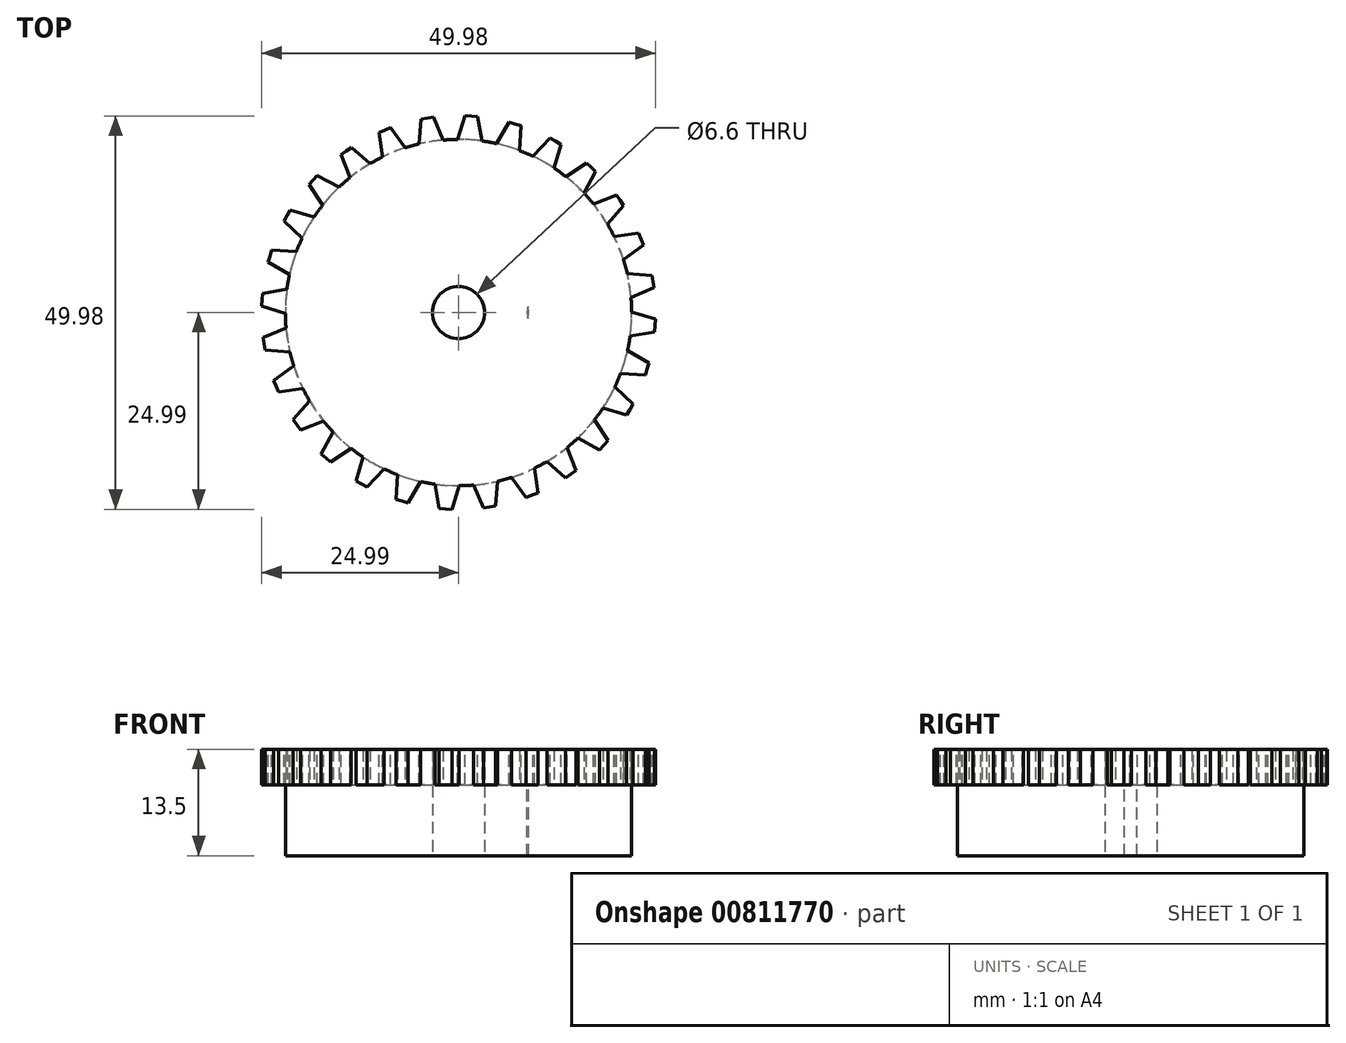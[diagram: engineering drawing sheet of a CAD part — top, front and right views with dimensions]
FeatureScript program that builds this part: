
annotation { "Feature Type Name" : "Feature", "Feature Type Description" : "" }
export const myFeature = defineFeature(function(context is Context, id is Id, definition is map)
    precondition{}
    {
        {
            var Q0;
            Q0=qCreatedBy(makeId("Top.planeOp"),FACE);
            var sketch = newSketch(context, id + "F0", { "sketchPlane" : qUnion([Q0])});
            skCircle(sketch, "E0", {"center": v(0, 0) * mm, "radius": 22 * mm});
            skLineSegment(sketch, "E1", {"start": v(-18.07, -12.55) * mm, "end": v(-20.53, -14.26) * mm, "construction": true});
            skLineSegment(sketch, "E2", {"start": v(-20.53, -14.26) * mm, "end": v(-20.07, -14.92) * mm});
            skLineSegment(sketch, "E3", {"start": v(-20.53, -14.26) * mm, "end": v(-20.99, -13.6) * mm});
            skLineSegment(sketch, "E4", {"start": v(-20.07, -14.92) * mm, "end": v(-17.6, -13.2) * mm, "construction": true});
            skLineSegment(sketch, "E5", {"start": v(-20.99, -13.6) * mm, "end": v(-18.51, -11.89) * mm, "construction": true});
            skLineSegment(sketch, "E6", {"start": v(-20.07, -14.92) * mm, "end": v(-17.14, -13.8) * mm});
            skLineSegment(sketch, "E7", {"start": v(-20.99, -13.6) * mm, "end": v(-18.9, -11.25) * mm});
            skCircle(sketch, "E8", {"center": v(0, 0) * mm, "radius": 8.87 * mm});
            skCircle(sketch, "E9", {"center": v(0, 0) * mm, "radius": 3.3 * mm});
            skLineSegment(sketch, "E10", {"start": v(-8.87, 0) * mm, "end": v(11.73, 0) * mm, "construction": true});
            skLineSegment(sketch, "E11.trimOffspring", {"start": v(-0.6, 8.85) * mm, "end": v(-0.6, 8.85) * mm});
            skCircle(sketch, "E12", {"center": v(11.73, 0) * mm, "radius": 3 * mm});
            skLineSegment(sketch, "E13", {"start": v(4.3, -7.76) * mm, "end": v(13.23, -2.6) * mm});
            skLineSegment(sketch, "E14.1.0", {"start": v(-17.43, -17.94) * mm, "end": v(-15.93, -15.17) * mm});
            skLineSegment(sketch, "E14.1.1", {"start": v(-17.43, -17.94) * mm, "end": v(-15.4, -15.7) * mm, "construction": true});
            skLineSegment(sketch, "E14.1.2", {"start": v(-14.82, -16.26) * mm, "end": v(-16.84, -18.47) * mm, "construction": true});
            skLineSegment(sketch, "E14.1.3", {"start": v(-16.25, -19.01) * mm, "end": v(-14.22, -16.79) * mm, "construction": true});
            skLineSegment(sketch, "E14.1.4", {"start": v(-16.25, -19.01) * mm, "end": v(-13.64, -17.26) * mm});
            skLineSegment(sketch, "E14.1.5", {"start": v(-16.84, -18.47) * mm, "end": v(-16.25, -19.01) * mm});
            skLineSegment(sketch, "E14.1.6", {"start": v(-16.84, -18.47) * mm, "end": v(-17.43, -17.94) * mm});
            skLineSegment(sketch, "E14.2.0", {"start": v(-13, -21.37) * mm, "end": v(-12.15, -18.34) * mm});
            skLineSegment(sketch, "E14.2.1", {"start": v(-13, -21.37) * mm, "end": v(-11.52, -18.74) * mm, "construction": true});
            skLineSegment(sketch, "E14.2.2", {"start": v(-10.83, -19.15) * mm, "end": v(-12.3, -21.76) * mm, "construction": true});
            skLineSegment(sketch, "E14.2.3", {"start": v(-11.61, -22.15) * mm, "end": v(-10.13, -19.53) * mm, "construction": true});
            skLineSegment(sketch, "E14.2.4", {"start": v(-11.61, -22.15) * mm, "end": v(-9.46, -19.86) * mm});
            skLineSegment(sketch, "E14.2.5", {"start": v(-12.3, -21.76) * mm, "end": v(-11.61, -22.15) * mm});
            skLineSegment(sketch, "E14.2.6", {"start": v(-12.3, -21.76) * mm, "end": v(-13, -21.37) * mm});
            skLineSegment(sketch, "E15.1.3.0", {"start": v(-7.93, -23.72) * mm, "end": v(-7.77, -20.58) * mm});
            skLineSegment(sketch, "E15.3.3.0", {"start": v(-7.93, -23.72) * mm, "end": v(-7.06, -20.84) * mm, "construction": true});
            skLineSegment(sketch, "E15.6.3.0", {"start": v(-6.3, -21.08) * mm, "end": v(-7.16, -23.95) * mm, "construction": true});
            skLineSegment(sketch, "E15.9.3.0", {"start": v(-6.4, -24.18) * mm, "end": v(-5.53, -21.3) * mm, "construction": true});
            skLineSegment(sketch, "E15.12.3.0", {"start": v(-6.4, -24.18) * mm, "end": v(-4.8, -21.47) * mm});
            skLineSegment(sketch, "E15.15.3.0", {"start": v(-7.16, -23.95) * mm, "end": v(-6.4, -24.18) * mm});
            skLineSegment(sketch, "E15.18.3.0", {"start": v(-7.16, -23.95) * mm, "end": v(-7.93, -23.72) * mm});
            skLineSegment(sketch, "E15.1.4.0", {"start": v(-2.45, -24.9) * mm, "end": v(-3, -21.8) * mm});
            skLineSegment(sketch, "E15.3.4.0", {"start": v(-2.45, -24.9) * mm, "end": v(-2.25, -21.88) * mm, "construction": true});
            skLineSegment(sketch, "E15.6.4.0", {"start": v(-1.45, -21.95) * mm, "end": v(-1.65, -24.95) * mm, "construction": true});
            skLineSegment(sketch, "E15.9.4.0", {"start": v(-0.85, -25) * mm, "end": v(-0.65, -22) * mm, "construction": true});
            skLineSegment(sketch, "E15.12.4.0", {"start": v(-0.85, -25) * mm, "end": v(0.1, -22) * mm});
            skLineSegment(sketch, "E15.15.4.0", {"start": v(-1.65, -24.95) * mm, "end": v(-0.85, -25) * mm});
            skLineSegment(sketch, "E15.18.4.0", {"start": v(-1.65, -24.95) * mm, "end": v(-2.45, -24.9) * mm});
            skLineSegment(sketch, "E15.1.5.0", {"start": v(3.15, -24.81) * mm, "end": v(1.93, -21.92) * mm});
            skLineSegment(sketch, "E15.3.5.0", {"start": v(3.15, -24.81) * mm, "end": v(2.68, -21.84) * mm, "construction": true});
            skLineSegment(sketch, "E15.6.5.0", {"start": v(3.47, -21.72) * mm, "end": v(3.94, -24.69) * mm, "construction": true});
            skLineSegment(sketch, "E15.9.5.0", {"start": v(4.73, -24.56) * mm, "end": v(4.26, -21.58) * mm, "construction": true});
            skLineSegment(sketch, "E15.12.5.0", {"start": v(4.73, -24.56) * mm, "end": v(5, -21.43) * mm});
            skLineSegment(sketch, "E15.15.5.0", {"start": v(3.94, -24.69) * mm, "end": v(4.73, -24.56) * mm});
            skLineSegment(sketch, "E15.18.5.0", {"start": v(3.94, -24.69) * mm, "end": v(3.15, -24.81) * mm});
            skLineSegment(sketch, "E15.1.6.0", {"start": v(8.6, -23.49) * mm, "end": v(6.76, -20.94) * mm});
            skLineSegment(sketch, "E15.3.6.0", {"start": v(8.6, -23.49) * mm, "end": v(7.47, -20.7) * mm, "construction": true});
            skLineSegment(sketch, "E15.6.6.0", {"start": v(8.22, -20.4) * mm, "end": v(9.34, -23.2) * mm, "construction": true});
            skLineSegment(sketch, "E15.9.6.0", {"start": v(10.08, -22.9) * mm, "end": v(8.95, -20.1) * mm, "construction": true});
            skLineSegment(sketch, "E15.12.6.0", {"start": v(10.08, -22.9) * mm, "end": v(9.63, -19.78) * mm});
            skLineSegment(sketch, "E15.15.6.0", {"start": v(9.34, -23.2) * mm, "end": v(10.08, -22.9) * mm});
            skLineSegment(sketch, "E15.18.6.0", {"start": v(9.34, -23.2) * mm, "end": v(8.6, -23.49) * mm});
            skLineSegment(sketch, "E15.1.7.0", {"start": v(13.6, -20.99) * mm, "end": v(11.25, -18.9) * mm});
            skLineSegment(sketch, "E15.3.7.0", {"start": v(13.6, -20.99) * mm, "end": v(11.89, -18.51) * mm, "construction": true});
            skLineSegment(sketch, "E15.6.7.0", {"start": v(12.55, -18.07) * mm, "end": v(14.26, -20.53) * mm, "construction": true});
            skLineSegment(sketch, "E15.9.7.0", {"start": v(14.92, -20.07) * mm, "end": v(13.2, -17.6) * mm, "construction": true});
            skLineSegment(sketch, "E15.12.7.0", {"start": v(14.92, -20.07) * mm, "end": v(13.8, -17.14) * mm});
            skLineSegment(sketch, "E15.15.7.0", {"start": v(14.26, -20.53) * mm, "end": v(14.92, -20.07) * mm});
            skLineSegment(sketch, "E15.18.7.0", {"start": v(14.26, -20.53) * mm, "end": v(13.6, -20.99) * mm});
            skLineSegment(sketch, "E15.1.8.0", {"start": v(17.94, -17.43) * mm, "end": v(15.17, -15.93) * mm});
            skLineSegment(sketch, "E15.3.8.0", {"start": v(17.94, -17.43) * mm, "end": v(15.7, -15.4) * mm, "construction": true});
            skLineSegment(sketch, "E15.6.8.0", {"start": v(16.26, -14.82) * mm, "end": v(18.47, -16.84) * mm, "construction": true});
            skLineSegment(sketch, "E15.9.8.0", {"start": v(19.01, -16.25) * mm, "end": v(16.79, -14.22) * mm, "construction": true});
            skLineSegment(sketch, "E15.12.8.0", {"start": v(19.01, -16.25) * mm, "end": v(17.26, -13.64) * mm});
            skLineSegment(sketch, "E15.15.8.0", {"start": v(18.47, -16.84) * mm, "end": v(19.01, -16.25) * mm});
            skLineSegment(sketch, "E15.18.8.0", {"start": v(18.47, -16.84) * mm, "end": v(17.94, -17.43) * mm});
            skLineSegment(sketch, "E15.1.9.0", {"start": v(21.37, -13) * mm, "end": v(18.34, -12.15) * mm});
            skLineSegment(sketch, "E15.3.9.0", {"start": v(21.37, -13) * mm, "end": v(18.74, -11.52) * mm, "construction": true});
            skLineSegment(sketch, "E15.6.9.0", {"start": v(19.15, -10.83) * mm, "end": v(21.76, -12.3) * mm, "construction": true});
            skLineSegment(sketch, "E15.9.9.0", {"start": v(22.15, -11.61) * mm, "end": v(19.53, -10.13) * mm, "construction": true});
            skLineSegment(sketch, "E15.12.9.0", {"start": v(22.15, -11.61) * mm, "end": v(19.86, -9.46) * mm});
            skLineSegment(sketch, "E15.15.9.0", {"start": v(21.76, -12.3) * mm, "end": v(22.15, -11.61) * mm});
            skLineSegment(sketch, "E15.18.9.0", {"start": v(21.76, -12.3) * mm, "end": v(21.37, -13) * mm});
            skLineSegment(sketch, "E15.1.10.0", {"start": v(23.72, -7.93) * mm, "end": v(20.58, -7.77) * mm});
            skLineSegment(sketch, "E15.3.10.0", {"start": v(23.72, -7.93) * mm, "end": v(20.84, -7.06) * mm, "construction": true});
            skLineSegment(sketch, "E15.6.10.0", {"start": v(21.08, -6.3) * mm, "end": v(23.95, -7.16) * mm, "construction": true});
            skLineSegment(sketch, "E15.9.10.0", {"start": v(24.18, -6.4) * mm, "end": v(21.3, -5.53) * mm, "construction": true});
            skLineSegment(sketch, "E15.12.10.0", {"start": v(24.18, -6.4) * mm, "end": v(21.47, -4.8) * mm});
            skLineSegment(sketch, "E15.15.10.0", {"start": v(23.95, -7.16) * mm, "end": v(24.18, -6.4) * mm});
            skLineSegment(sketch, "E15.18.10.0", {"start": v(23.95, -7.16) * mm, "end": v(23.72, -7.93) * mm});
            skLineSegment(sketch, "E15.1.11.0", {"start": v(24.9, -2.45) * mm, "end": v(21.8, -3) * mm});
            skLineSegment(sketch, "E15.3.11.0", {"start": v(24.9, -2.45) * mm, "end": v(21.88, -2.25) * mm, "construction": true});
            skLineSegment(sketch, "E15.6.11.0", {"start": v(21.95, -1.45) * mm, "end": v(24.95, -1.65) * mm, "construction": true});
            skLineSegment(sketch, "E15.9.11.0", {"start": v(25, -0.85) * mm, "end": v(22, -0.65) * mm, "construction": true});
            skLineSegment(sketch, "E15.12.11.0", {"start": v(25, -0.85) * mm, "end": v(22, 0.1) * mm});
            skLineSegment(sketch, "E15.15.11.0", {"start": v(24.95, -1.65) * mm, "end": v(25, -0.85) * mm});
            skLineSegment(sketch, "E15.18.11.0", {"start": v(24.95, -1.65) * mm, "end": v(24.9, -2.45) * mm});
            skLineSegment(sketch, "E15.1.12.0", {"start": v(24.81, 3.15) * mm, "end": v(21.92, 1.93) * mm});
            skLineSegment(sketch, "E15.3.12.0", {"start": v(24.81, 3.15) * mm, "end": v(21.84, 2.68) * mm, "construction": true});
            skLineSegment(sketch, "E15.6.12.0", {"start": v(21.72, 3.47) * mm, "end": v(24.69, 3.94) * mm, "construction": true});
            skLineSegment(sketch, "E15.9.12.0", {"start": v(24.56, 4.73) * mm, "end": v(21.58, 4.26) * mm, "construction": true});
            skLineSegment(sketch, "E15.12.12.0", {"start": v(24.56, 4.73) * mm, "end": v(21.43, 5) * mm});
            skLineSegment(sketch, "E15.15.12.0", {"start": v(24.69, 3.94) * mm, "end": v(24.56, 4.73) * mm});
            skLineSegment(sketch, "E15.18.12.0", {"start": v(24.69, 3.94) * mm, "end": v(24.81, 3.15) * mm});
            skLineSegment(sketch, "E15.1.13.0", {"start": v(23.49, 8.6) * mm, "end": v(20.94, 6.76) * mm});
            skLineSegment(sketch, "E15.3.13.0", {"start": v(23.49, 8.6) * mm, "end": v(20.7, 7.47) * mm, "construction": true});
            skLineSegment(sketch, "E15.6.13.0", {"start": v(20.4, 8.22) * mm, "end": v(23.2, 9.34) * mm, "construction": true});
            skLineSegment(sketch, "E15.9.13.0", {"start": v(22.9, 10.08) * mm, "end": v(20.1, 8.95) * mm, "construction": true});
            skLineSegment(sketch, "E15.12.13.0", {"start": v(22.9, 10.08) * mm, "end": v(19.78, 9.63) * mm});
            skLineSegment(sketch, "E15.15.13.0", {"start": v(23.2, 9.34) * mm, "end": v(22.9, 10.08) * mm});
            skLineSegment(sketch, "E15.18.13.0", {"start": v(23.2, 9.34) * mm, "end": v(23.49, 8.6) * mm});
            skLineSegment(sketch, "E15.1.14.0", {"start": v(20.99, 13.6) * mm, "end": v(18.9, 11.25) * mm});
            skLineSegment(sketch, "E15.3.14.0", {"start": v(20.99, 13.6) * mm, "end": v(18.51, 11.89) * mm, "construction": true});
            skLineSegment(sketch, "E15.6.14.0", {"start": v(18.07, 12.55) * mm, "end": v(20.53, 14.26) * mm, "construction": true});
            skLineSegment(sketch, "E15.9.14.0", {"start": v(20.07, 14.92) * mm, "end": v(17.6, 13.2) * mm, "construction": true});
            skLineSegment(sketch, "E15.12.14.0", {"start": v(20.07, 14.92) * mm, "end": v(17.14, 13.8) * mm});
            skLineSegment(sketch, "E15.15.14.0", {"start": v(20.53, 14.26) * mm, "end": v(20.07, 14.92) * mm});
            skLineSegment(sketch, "E15.18.14.0", {"start": v(20.53, 14.26) * mm, "end": v(20.99, 13.6) * mm});
            skLineSegment(sketch, "E15.1.15.0", {"start": v(17.43, 17.94) * mm, "end": v(15.93, 15.17) * mm});
            skLineSegment(sketch, "E15.3.15.0", {"start": v(17.43, 17.94) * mm, "end": v(15.4, 15.7) * mm, "construction": true});
            skLineSegment(sketch, "E15.6.15.0", {"start": v(14.82, 16.26) * mm, "end": v(16.84, 18.47) * mm, "construction": true});
            skLineSegment(sketch, "E15.9.15.0", {"start": v(16.25, 19.01) * mm, "end": v(14.22, 16.79) * mm, "construction": true});
            skLineSegment(sketch, "E15.12.15.0", {"start": v(16.25, 19.01) * mm, "end": v(13.64, 17.26) * mm});
            skLineSegment(sketch, "E15.15.15.0", {"start": v(16.84, 18.47) * mm, "end": v(16.25, 19.01) * mm});
            skLineSegment(sketch, "E15.18.15.0", {"start": v(16.84, 18.47) * mm, "end": v(17.43, 17.94) * mm});
            skLineSegment(sketch, "E15.1.16.0", {"start": v(13, 21.37) * mm, "end": v(12.15, 18.34) * mm});
            skLineSegment(sketch, "E15.3.16.0", {"start": v(13, 21.37) * mm, "end": v(11.52, 18.74) * mm, "construction": true});
            skLineSegment(sketch, "E15.6.16.0", {"start": v(10.83, 19.15) * mm, "end": v(12.3, 21.76) * mm, "construction": true});
            skLineSegment(sketch, "E15.9.16.0", {"start": v(11.61, 22.15) * mm, "end": v(10.13, 19.53) * mm, "construction": true});
            skLineSegment(sketch, "E15.12.16.0", {"start": v(11.61, 22.15) * mm, "end": v(9.46, 19.86) * mm});
            skLineSegment(sketch, "E15.15.16.0", {"start": v(12.3, 21.76) * mm, "end": v(11.61, 22.15) * mm});
            skLineSegment(sketch, "E15.18.16.0", {"start": v(12.3, 21.76) * mm, "end": v(13, 21.37) * mm});
            skLineSegment(sketch, "E15.1.17.0", {"start": v(7.93, 23.72) * mm, "end": v(7.77, 20.58) * mm});
            skLineSegment(sketch, "E15.3.17.0", {"start": v(7.93, 23.72) * mm, "end": v(7.06, 20.84) * mm, "construction": true});
            skLineSegment(sketch, "E15.6.17.0", {"start": v(6.3, 21.08) * mm, "end": v(7.16, 23.95) * mm, "construction": true});
            skLineSegment(sketch, "E15.9.17.0", {"start": v(6.4, 24.18) * mm, "end": v(5.53, 21.3) * mm, "construction": true});
            skLineSegment(sketch, "E15.12.17.0", {"start": v(6.4, 24.18) * mm, "end": v(4.8, 21.47) * mm});
            skLineSegment(sketch, "E15.15.17.0", {"start": v(7.16, 23.95) * mm, "end": v(6.4, 24.18) * mm});
            skLineSegment(sketch, "E15.18.17.0", {"start": v(7.16, 23.95) * mm, "end": v(7.93, 23.72) * mm});
            skLineSegment(sketch, "E15.1.18.0", {"start": v(2.45, 24.9) * mm, "end": v(3, 21.8) * mm});
            skLineSegment(sketch, "E15.3.18.0", {"start": v(2.45, 24.9) * mm, "end": v(2.25, 21.88) * mm, "construction": true});
            skLineSegment(sketch, "E15.6.18.0", {"start": v(1.45, 21.95) * mm, "end": v(1.65, 24.95) * mm, "construction": true});
            skLineSegment(sketch, "E15.9.18.0", {"start": v(0.85, 25) * mm, "end": v(0.65, 22) * mm, "construction": true});
            skLineSegment(sketch, "E15.12.18.0", {"start": v(0.85, 25) * mm, "end": v(-0.1, 22) * mm});
            skLineSegment(sketch, "E15.15.18.0", {"start": v(1.65, 24.95) * mm, "end": v(0.85, 25) * mm});
            skLineSegment(sketch, "E15.18.18.0", {"start": v(1.65, 24.95) * mm, "end": v(2.45, 24.9) * mm});
            skLineSegment(sketch, "E15.1.19.0", {"start": v(-3.15, 24.81) * mm, "end": v(-1.93, 21.92) * mm});
            skLineSegment(sketch, "E15.3.19.0", {"start": v(-3.15, 24.81) * mm, "end": v(-2.68, 21.84) * mm, "construction": true});
            skLineSegment(sketch, "E15.6.19.0", {"start": v(-3.47, 21.72) * mm, "end": v(-3.94, 24.69) * mm, "construction": true});
            skLineSegment(sketch, "E15.9.19.0", {"start": v(-4.73, 24.56) * mm, "end": v(-4.26, 21.58) * mm, "construction": true});
            skLineSegment(sketch, "E15.12.19.0", {"start": v(-4.73, 24.56) * mm, "end": v(-5, 21.43) * mm});
            skLineSegment(sketch, "E15.15.19.0", {"start": v(-3.94, 24.69) * mm, "end": v(-4.73, 24.56) * mm});
            skLineSegment(sketch, "E15.18.19.0", {"start": v(-3.94, 24.69) * mm, "end": v(-3.15, 24.81) * mm});
            skLineSegment(sketch, "E15.1.20.0", {"start": v(-8.6, 23.49) * mm, "end": v(-6.76, 20.94) * mm});
            skLineSegment(sketch, "E15.3.20.0", {"start": v(-8.6, 23.49) * mm, "end": v(-7.47, 20.7) * mm, "construction": true});
            skLineSegment(sketch, "E15.6.20.0", {"start": v(-8.22, 20.4) * mm, "end": v(-9.34, 23.2) * mm, "construction": true});
            skLineSegment(sketch, "E15.9.20.0", {"start": v(-10.08, 22.9) * mm, "end": v(-8.95, 20.1) * mm, "construction": true});
            skLineSegment(sketch, "E15.12.20.0", {"start": v(-10.08, 22.9) * mm, "end": v(-9.63, 19.78) * mm});
            skLineSegment(sketch, "E15.15.20.0", {"start": v(-9.34, 23.2) * mm, "end": v(-10.08, 22.9) * mm});
            skLineSegment(sketch, "E15.18.20.0", {"start": v(-9.34, 23.2) * mm, "end": v(-8.6, 23.49) * mm});
            skLineSegment(sketch, "E15.1.21.0", {"start": v(-13.6, 20.99) * mm, "end": v(-11.25, 18.9) * mm});
            skLineSegment(sketch, "E15.3.21.0", {"start": v(-13.6, 20.99) * mm, "end": v(-11.89, 18.51) * mm, "construction": true});
            skLineSegment(sketch, "E15.6.21.0", {"start": v(-12.55, 18.07) * mm, "end": v(-14.26, 20.53) * mm, "construction": true});
            skLineSegment(sketch, "E15.9.21.0", {"start": v(-14.92, 20.07) * mm, "end": v(-13.2, 17.6) * mm, "construction": true});
            skLineSegment(sketch, "E15.12.21.0", {"start": v(-14.92, 20.07) * mm, "end": v(-13.8, 17.14) * mm});
            skLineSegment(sketch, "E15.15.21.0", {"start": v(-14.26, 20.53) * mm, "end": v(-14.92, 20.07) * mm});
            skLineSegment(sketch, "E15.18.21.0", {"start": v(-14.26, 20.53) * mm, "end": v(-13.6, 20.99) * mm});
            skLineSegment(sketch, "E15.1.22.0", {"start": v(-17.94, 17.43) * mm, "end": v(-15.17, 15.93) * mm});
            skLineSegment(sketch, "E15.3.22.0", {"start": v(-17.94, 17.43) * mm, "end": v(-15.7, 15.4) * mm, "construction": true});
            skLineSegment(sketch, "E15.6.22.0", {"start": v(-16.26, 14.82) * mm, "end": v(-18.47, 16.84) * mm, "construction": true});
            skLineSegment(sketch, "E15.9.22.0", {"start": v(-19.01, 16.25) * mm, "end": v(-16.79, 14.22) * mm, "construction": true});
            skLineSegment(sketch, "E15.12.22.0", {"start": v(-19.01, 16.25) * mm, "end": v(-17.26, 13.64) * mm});
            skLineSegment(sketch, "E15.15.22.0", {"start": v(-18.47, 16.84) * mm, "end": v(-19.01, 16.25) * mm});
            skLineSegment(sketch, "E15.18.22.0", {"start": v(-18.47, 16.84) * mm, "end": v(-17.94, 17.43) * mm});
            skLineSegment(sketch, "E15.1.23.0", {"start": v(-21.37, 13) * mm, "end": v(-18.34, 12.15) * mm});
            skLineSegment(sketch, "E15.3.23.0", {"start": v(-21.37, 13) * mm, "end": v(-18.74, 11.52) * mm, "construction": true});
            skLineSegment(sketch, "E15.6.23.0", {"start": v(-19.15, 10.83) * mm, "end": v(-21.76, 12.3) * mm, "construction": true});
            skLineSegment(sketch, "E15.9.23.0", {"start": v(-22.15, 11.61) * mm, "end": v(-19.53, 10.13) * mm, "construction": true});
            skLineSegment(sketch, "E15.12.23.0", {"start": v(-22.15, 11.61) * mm, "end": v(-19.86, 9.46) * mm});
            skLineSegment(sketch, "E15.15.23.0", {"start": v(-21.76, 12.3) * mm, "end": v(-22.15, 11.61) * mm});
            skLineSegment(sketch, "E15.18.23.0", {"start": v(-21.76, 12.3) * mm, "end": v(-21.37, 13) * mm});
            skLineSegment(sketch, "E15.1.24.0", {"start": v(-23.72, 7.93) * mm, "end": v(-20.58, 7.77) * mm});
            skLineSegment(sketch, "E15.3.24.0", {"start": v(-23.72, 7.93) * mm, "end": v(-20.84, 7.06) * mm, "construction": true});
            skLineSegment(sketch, "E15.6.24.0", {"start": v(-21.08, 6.3) * mm, "end": v(-23.95, 7.16) * mm, "construction": true});
            skLineSegment(sketch, "E15.9.24.0", {"start": v(-24.18, 6.4) * mm, "end": v(-21.3, 5.53) * mm, "construction": true});
            skLineSegment(sketch, "E15.12.24.0", {"start": v(-24.18, 6.4) * mm, "end": v(-21.47, 4.8) * mm});
            skLineSegment(sketch, "E15.15.24.0", {"start": v(-23.95, 7.16) * mm, "end": v(-24.18, 6.4) * mm});
            skLineSegment(sketch, "E15.18.24.0", {"start": v(-23.95, 7.16) * mm, "end": v(-23.72, 7.93) * mm});
            skLineSegment(sketch, "E15.1.25.0", {"start": v(-24.9, 2.45) * mm, "end": v(-21.8, 3) * mm});
            skLineSegment(sketch, "E15.3.25.0", {"start": v(-24.9, 2.45) * mm, "end": v(-21.88, 2.25) * mm, "construction": true});
            skLineSegment(sketch, "E15.6.25.0", {"start": v(-21.95, 1.45) * mm, "end": v(-24.95, 1.65) * mm, "construction": true});
            skLineSegment(sketch, "E15.9.25.0", {"start": v(-25, 0.85) * mm, "end": v(-22, 0.65) * mm, "construction": true});
            skLineSegment(sketch, "E15.12.25.0", {"start": v(-25, 0.85) * mm, "end": v(-22, -0.1) * mm});
            skLineSegment(sketch, "E15.15.25.0", {"start": v(-24.95, 1.65) * mm, "end": v(-25, 0.85) * mm});
            skLineSegment(sketch, "E15.18.25.0", {"start": v(-24.95, 1.65) * mm, "end": v(-24.9, 2.45) * mm});
            skLineSegment(sketch, "E15.1.26.0", {"start": v(-24.81, -3.15) * mm, "end": v(-21.92, -1.93) * mm});
            skLineSegment(sketch, "E15.3.26.0", {"start": v(-24.81, -3.15) * mm, "end": v(-21.84, -2.68) * mm, "construction": true});
            skLineSegment(sketch, "E15.6.26.0", {"start": v(-21.72, -3.47) * mm, "end": v(-24.69, -3.94) * mm, "construction": true});
            skLineSegment(sketch, "E15.9.26.0", {"start": v(-24.56, -4.73) * mm, "end": v(-21.58, -4.26) * mm, "construction": true});
            skLineSegment(sketch, "E15.12.26.0", {"start": v(-24.56, -4.73) * mm, "end": v(-21.43, -5) * mm});
            skLineSegment(sketch, "E15.15.26.0", {"start": v(-24.69, -3.94) * mm, "end": v(-24.56, -4.73) * mm});
            skLineSegment(sketch, "E15.18.26.0", {"start": v(-24.69, -3.94) * mm, "end": v(-24.81, -3.15) * mm});
            skLineSegment(sketch, "E15.1.27.0", {"start": v(-23.49, -8.6) * mm, "end": v(-20.94, -6.76) * mm});
            skLineSegment(sketch, "E15.3.27.0", {"start": v(-23.49, -8.6) * mm, "end": v(-20.7, -7.47) * mm, "construction": true});
            skLineSegment(sketch, "E15.6.27.0", {"start": v(-20.4, -8.22) * mm, "end": v(-23.2, -9.34) * mm, "construction": true});
            skLineSegment(sketch, "E15.9.27.0", {"start": v(-22.9, -10.08) * mm, "end": v(-20.1, -8.95) * mm, "construction": true});
            skLineSegment(sketch, "E15.12.27.0", {"start": v(-22.9, -10.08) * mm, "end": v(-19.78, -9.63) * mm});
            skLineSegment(sketch, "E15.15.27.0", {"start": v(-23.2, -9.34) * mm, "end": v(-22.9, -10.08) * mm});
            skLineSegment(sketch, "E15.18.27.0", {"start": v(-23.2, -9.34) * mm, "end": v(-23.49, -8.6) * mm});
            skLineSegment(sketch, "E16", {"start": v(4.3, -7.76) * mm, "end": v(4.3, 7.76) * mm, "construction": true});
            skLineSegment(sketch, "E17", {"start": v(4.3, 7.76) * mm, "end": v(13.23, 2.6) * mm});
            skSolve(sketch);
        }
        {
            var Q0;
            {var subQ0=sQuery(id+"F0.wireOp",EDGE,"E15.1.20.0");Q0=makeQuery(id+"F0.imprint","IMPRINT",FACE,{"disambiguationData":[TD([[makeQuery(id+"F0.imprint","IMPRINT",EDGE,{"derivedFrom":subQ0}),-1.0]])]});}
            var Q1;
            {var subQ0=sQuery(id+"F0.wireOp",EDGE,"E12");var subQ1=makeQuery(id+"F0.imprint","INTERSECT",VERTEX,{"derivedFrom":[subQ0,sQuery(id+"F0.wireOp",EDGE,"KuiEAQZw-HmBo-JUDk-2FJ1-OJibavO7FM1e")]});Q1=makeQuery(id+"F0.imprint","IMPRINT",FACE,{"disambiguationData":[TD([[makeQuery(id+"F0.imprint","IMPRINT",EDGE,{"disambiguationData":[TD([[subQ1,-1.0]])],"derivedFrom":subQ0}),1.0]])]});}
            var Q2;
            {var subQ1=sQuery(id+"F0.wireOp",EDGE,"E15.1.22.0");Q2=makeQuery(id+"F0.imprint","IMPRINT",FACE,{"disambiguationData":[TD([[makeQuery(id+"F0.imprint","IMPRINT",EDGE,{"derivedFrom":subQ1}),-1.0]])]});}
            var Q3;
            {var subQ1=sQuery(id+"F0.wireOp",EDGE,"E15.1.14.0");Q3=makeQuery(id+"F0.imprint","IMPRINT",FACE,{"disambiguationData":[TD([[makeQuery(id+"F0.imprint","IMPRINT",EDGE,{"derivedFrom":subQ1}),-1.0]])]});}
            var Q4;
            {var subQ1=sQuery(id+"F0.wireOp",EDGE,"E15.1.24.0");Q4=makeQuery(id+"F0.imprint","IMPRINT",FACE,{"disambiguationData":[TD([[makeQuery(id+"F0.imprint","IMPRINT",EDGE,{"derivedFrom":subQ1}),-1.0]])]});}
            var Q5;
            {var subQ1=sQuery(id+"F0.wireOp",EDGE,"E15.1.13.0");Q5=makeQuery(id+"F0.imprint","IMPRINT",FACE,{"disambiguationData":[TD([[makeQuery(id+"F0.imprint","IMPRINT",EDGE,{"derivedFrom":subQ1}),-1.0]])]});}
            var Q6;
            {var subQ1=sQuery(id+"F0.wireOp",EDGE,"E15.1.4.0");Q6=makeQuery(id+"F0.imprint","IMPRINT",FACE,{"disambiguationData":[TD([[makeQuery(id+"F0.imprint","IMPRINT",EDGE,{"derivedFrom":subQ1}),-1.0]])]});}
            var Q7;
            {var subQ1=sQuery(id+"F0.wireOp",EDGE,"E15.1.12.0");Q7=makeQuery(id+"F0.imprint","IMPRINT",FACE,{"disambiguationData":[TD([[makeQuery(id+"F0.imprint","IMPRINT",EDGE,{"derivedFrom":subQ1}),-1.0]])]});}
            var Q8;
            {var subQ0=sQuery(id+"F0.wireOp",EDGE,"E15.1.8.0");Q8=makeQuery(id+"F0.imprint","IMPRINT",FACE,{"disambiguationData":[TD([[makeQuery(id+"F0.imprint","IMPRINT",EDGE,{"derivedFrom":subQ0}),-1.0]])]});}
            var Q9;
            Q9=makeQuery(id+"F0.imprint","IMPRINT",FACE,{"disambiguationData":[TD([[makeQuery(id+"F0.imprint","IMPRINT",EDGE,{"derivedFrom":sQuery(id+"F0.wireOp",EDGE,"E2")}),1.0]])]});
            var Q10;
            Q10=makeQuery(id+"F0.imprint","IMPRINT",FACE,{"disambiguationData":[TD([[makeQuery(id+"F0.imprint","IMPRINT",EDGE,{"derivedFrom":sQuery(id+"F0.wireOp",EDGE,"E9")}),-1.0]])]});
            var Q11;
            {var subQ1=sQuery(id+"F0.wireOp",EDGE,"E15.1.27.0");Q11=makeQuery(id+"F0.imprint","IMPRINT",FACE,{"disambiguationData":[TD([[makeQuery(id+"F0.imprint","IMPRINT",EDGE,{"derivedFrom":subQ1}),-1.0]])]});}
            var Q12;
            {var subQ1=sQuery(id+"F0.wireOp",EDGE,"E15.1.26.0");Q12=makeQuery(id+"F0.imprint","IMPRINT",FACE,{"disambiguationData":[TD([[makeQuery(id+"F0.imprint","IMPRINT",EDGE,{"derivedFrom":subQ1}),-1.0]])]});}
            var Q13;
            {var subQ1=sQuery(id+"F0.wireOp",EDGE,"E14.1.0");Q13=makeQuery(id+"F0.imprint","IMPRINT",FACE,{"disambiguationData":[TD([[makeQuery(id+"F0.imprint","IMPRINT",EDGE,{"derivedFrom":subQ1}),-1.0]])]});}
            var Q14;
            {var subQ1=sQuery(id+"F0.wireOp",EDGE,"E15.1.21.0");Q14=makeQuery(id+"F0.imprint","IMPRINT",FACE,{"disambiguationData":[TD([[makeQuery(id+"F0.imprint","IMPRINT",EDGE,{"derivedFrom":subQ1}),-1.0]])]});}
            var Q15;
            {var subQ0=sQuery(id+"F0.wireOp",EDGE,"KuiEAQZw-HmBo-JUDk-2FJ1-OJibavO7FM1e");var subQ1=sQuery(id+"F0.wireOp",EDGE,"E8");var subQ2=makeQuery(id+"F0.imprint","INTERSECT",VERTEX,{"derivedFrom":[subQ1,subQ0]});Q15=makeQuery(id+"F0.imprint","IMPRINT",FACE,{"disambiguationData":[TD([[makeQuery(id+"F0.imprint","IMPRINT",EDGE,{"disambiguationData":[TD([[subQ2,1.0]])],"derivedFrom":subQ1}),-1.0]])]});}
            var Q16;
            {var subQ0=sQuery(id+"F0.wireOp",EDGE,"E14.2.0");Q16=makeQuery(id+"F0.imprint","IMPRINT",FACE,{"disambiguationData":[TD([[makeQuery(id+"F0.imprint","IMPRINT",EDGE,{"derivedFrom":subQ0}),-1.0]])]});}
            var Q17;
            {var subQ1=sQuery(id+"F0.wireOp",EDGE,"E15.1.7.0");Q17=makeQuery(id+"F0.imprint","IMPRINT",FACE,{"disambiguationData":[TD([[makeQuery(id+"F0.imprint","IMPRINT",EDGE,{"derivedFrom":subQ1}),-1.0]])]});}
            var Q18;
            {var subQ0=sQuery(id+"F0.wireOp",EDGE,"E0");var subQ33=makeQuery(id+"F0.imprint","INTERSECT",VERTEX,{"derivedFrom":[subQ0,sQuery(id+"F0.wireOp",EDGE,"E15.12.11.0")]});Q18=makeQuery(id+"F0.imprint","IMPRINT",FACE,{"disambiguationData":[TD([[makeQuery(id+"F0.imprint","IMPRINT",EDGE,{"disambiguationData":[TD([[subQ33,-1.0]])],"derivedFrom":subQ0}),1.0]])]});}
            var Q19;
            {var subQ0=sQuery(id+"F0.wireOp",EDGE,"E15.1.25.0");Q19=makeQuery(id+"F0.imprint","IMPRINT",FACE,{"disambiguationData":[TD([[makeQuery(id+"F0.imprint","IMPRINT",EDGE,{"derivedFrom":subQ0}),-1.0]])]});}
            var Q20;
            {var subQ0=sQuery(id+"F0.wireOp",EDGE,"E15.1.15.0");Q20=makeQuery(id+"F0.imprint","IMPRINT",FACE,{"disambiguationData":[TD([[makeQuery(id+"F0.imprint","IMPRINT",EDGE,{"derivedFrom":subQ0}),-1.0]])]});}
            var Q21;
            {var subQ1=sQuery(id+"F0.wireOp",EDGE,"E15.1.9.0");Q21=makeQuery(id+"F0.imprint","IMPRINT",FACE,{"disambiguationData":[TD([[makeQuery(id+"F0.imprint","IMPRINT",EDGE,{"derivedFrom":subQ1}),-1.0]])]});}
            var Q22;
            {var subQ1=sQuery(id+"F0.wireOp",EDGE,"E15.1.5.0");Q22=makeQuery(id+"F0.imprint","IMPRINT",FACE,{"disambiguationData":[TD([[makeQuery(id+"F0.imprint","IMPRINT",EDGE,{"derivedFrom":subQ1}),-1.0]])]});}
            var Q23;
            {var subQ1=sQuery(id+"F0.wireOp",EDGE,"E15.1.16.0");Q23=makeQuery(id+"F0.imprint","IMPRINT",FACE,{"disambiguationData":[TD([[makeQuery(id+"F0.imprint","IMPRINT",EDGE,{"derivedFrom":subQ1}),-1.0]])]});}
            var Q24;
            {var subQ1=sQuery(id+"F0.wireOp",EDGE,"E15.1.17.0");Q24=makeQuery(id+"F0.imprint","IMPRINT",FACE,{"disambiguationData":[TD([[makeQuery(id+"F0.imprint","IMPRINT",EDGE,{"derivedFrom":subQ1}),-1.0]])]});}
            var Q25;
            {var subQ1=sQuery(id+"F0.wireOp",EDGE,"E15.1.19.0");Q25=makeQuery(id+"F0.imprint","IMPRINT",FACE,{"disambiguationData":[TD([[makeQuery(id+"F0.imprint","IMPRINT",EDGE,{"derivedFrom":subQ1}),-1.0]])]});}
            var Q26;
            {var subQ1=sQuery(id+"F0.wireOp",EDGE,"E15.1.23.0");Q26=makeQuery(id+"F0.imprint","IMPRINT",FACE,{"disambiguationData":[TD([[makeQuery(id+"F0.imprint","IMPRINT",EDGE,{"derivedFrom":subQ1}),-1.0]])]});}
            var Q27;
            {var subQ1=sQuery(id+"F0.wireOp",EDGE,"E15.1.6.0");Q27=makeQuery(id+"F0.imprint","IMPRINT",FACE,{"disambiguationData":[TD([[makeQuery(id+"F0.imprint","IMPRINT",EDGE,{"derivedFrom":subQ1}),-1.0]])]});}
            var Q28;
            {var subQ0=sQuery(id+"F0.wireOp",EDGE,"E15.1.3.0");Q28=makeQuery(id+"F0.imprint","IMPRINT",FACE,{"disambiguationData":[TD([[makeQuery(id+"F0.imprint","IMPRINT",EDGE,{"derivedFrom":subQ0}),-1.0]])]});}
            var Q29;
            {var subQ0=sQuery(id+"F0.wireOp",EDGE,"E15.1.18.0");Q29=makeQuery(id+"F0.imprint","IMPRINT",FACE,{"disambiguationData":[TD([[makeQuery(id+"F0.imprint","IMPRINT",EDGE,{"derivedFrom":subQ0}),-1.0]])]});}
            var Q30;
            {var subQ1=sQuery(id+"F0.wireOp",EDGE,"E15.1.11.0");Q30=makeQuery(id+"F0.imprint","IMPRINT",FACE,{"disambiguationData":[TD([[makeQuery(id+"F0.imprint","IMPRINT",EDGE,{"derivedFrom":subQ1}),-1.0]])]});}
            var Q31;
            {var subQ1=sQuery(id+"F0.wireOp",EDGE,"E15.1.10.0");Q31=makeQuery(id+"F0.imprint","IMPRINT",FACE,{"disambiguationData":[TD([[makeQuery(id+"F0.imprint","IMPRINT",EDGE,{"derivedFrom":subQ1}),-1.0]])]});}
            var Q32;
            {var subQ0=sQuery(id+"F0.wireOp",EDGE,"E13");var subQ1=sQuery(id+"F0.wireOp",EDGE,"E8");var subQ3=makeQuery(id+"F0.imprint","INTERSECT",VERTEX,{"derivedFrom":[subQ1,subQ0]});Q32=makeQuery(id+"F0.imprint","IMPRINT",FACE,{"disambiguationData":[TD([[makeQuery(id+"F0.imprint","IMPRINT",EDGE,{"disambiguationData":[TD([[subQ3,1.0]])],"derivedFrom":subQ1}),1.0]])]});}
            var Q33;
            {var subQ0=sQuery(id+"F0.wireOp",EDGE,"E11.trimOffspring");Q33=makeQuery(id+"F0.imprint","IMPRINT",FACE,{"disambiguationData":[TD([[makeQuery(id+"F0.imprint","IMPRINT",EDGE,{"derivedFrom":subQ0}),-1.0]])]});}
            var Q34;
            {var subQ0=sQuery(id+"F0.wireOp",EDGE,"KuiEAQZw-HmBo-JUDk-2FJ1-OJibavO7FM1e");var subQ1=sQuery(id+"F0.wireOp",EDGE,"E8");var subQ3=makeQuery(id+"F0.imprint","INTERSECT",VERTEX,{"derivedFrom":[subQ1,subQ0]});Q34=makeQuery(id+"F0.imprint","IMPRINT",FACE,{"disambiguationData":[TD([[makeQuery(id+"F0.imprint","IMPRINT",EDGE,{"disambiguationData":[TD([[subQ3,-1.0]])],"derivedFrom":subQ1}),1.0]])]});}
            var Q35;
            {var subQ0=sQuery(id+"F0.wireOp",EDGE,"8zvVGQID-yt3e-UfqD-yb9D-NtDXdwGmcpxK");Q35=makeQuery(id+"F0.imprint","IMPRINT",FACE,{"disambiguationData":[TD([[makeQuery(id+"F0.imprint","IMPRINT",EDGE,{"derivedFrom":subQ0}),-1.0]])]});}
            var Q36;
            {var subQ0=sQuery(id+"F0.wireOp",EDGE,"E17");var subQ1=sQuery(id+"F0.wireOp",EDGE,"E8");var subQ2=makeQuery(id+"F0.imprint","INTERSECT",VERTEX,{"disambiguationData":[OD(1.0)],"derivedFrom":[subQ1,subQ0]});Q36=makeQuery(id+"F0.imprint","IMPRINT",FACE,{"disambiguationData":[TD([[makeQuery(id+"F0.imprint","IMPRINT",EDGE,{"disambiguationData":[TD([[subQ2,1.0]])],"derivedFrom":subQ1}),-1.0]])]});}
            var Q37;
            {var subQ0=sQuery(id+"F0.wireOp",EDGE,"E13");var subQ1=sQuery(id+"F0.wireOp",EDGE,"E8");var subQ2=makeQuery(id+"F0.imprint","INTERSECT",VERTEX,{"disambiguationData":[OD(1.0)],"derivedFrom":[subQ1,subQ0]});Q37=makeQuery(id+"F0.imprint","IMPRINT",FACE,{"disambiguationData":[TD([[makeQuery(id+"F0.imprint","IMPRINT",EDGE,{"disambiguationData":[TD([[subQ2,-1.0]])],"derivedFrom":subQ1}),-1.0]])]});}
            extrude(context, id + "F1", {"entities" : qUnion([Q0, Q1, Q2, Q3, Q4, Q5, Q6, Q7, Q8, Q9, Q10, Q11, Q12, Q13, Q14, Q15, Q16, Q17, Q18, Q19, Q20, Q21, Q22, Q23, Q24, Q25, Q26, Q27, Q28, Q29, Q30, Q31, Q32, Q33, Q34, Q35, Q36, Q37]), "depth" : 4.5 * mm, "offsetDistance" : 25 * mm});
        }
        {
            var Q0;
            {var subQ0=sQuery(id+"F0.wireOp",EDGE,"E17");var subQ1=sQuery(id+"F0.wireOp",EDGE,"E8");var subQ2=makeQuery(id+"F0.imprint","INTERSECT",VERTEX,{"disambiguationData":[OD(1.0)],"derivedFrom":[subQ1,subQ0]});Q0=makeQuery(id+"F0.imprint","IMPRINT",FACE,{"disambiguationData":[TD([[makeQuery(id+"F0.imprint","IMPRINT",EDGE,{"disambiguationData":[TD([[subQ2,1.0]])],"derivedFrom":subQ1}),-1.0]])]});}
            var Q1;
            {var subQ0=sQuery(id+"F0.wireOp",EDGE,"E13");var subQ1=sQuery(id+"F0.wireOp",EDGE,"E8");var subQ2=makeQuery(id+"F0.imprint","INTERSECT",VERTEX,{"disambiguationData":[OD(1.0)],"derivedFrom":[subQ1,subQ0]});Q1=makeQuery(id+"F0.imprint","IMPRINT",FACE,{"disambiguationData":[TD([[makeQuery(id+"F0.imprint","IMPRINT",EDGE,{"disambiguationData":[TD([[subQ2,-1.0]])],"derivedFrom":subQ1}),-1.0]])]});}
            var Q2;
            {var subQ0=sQuery(id+"F0.wireOp",EDGE,"E12");var subQ1=sQuery(id+"F0.wireOp",EDGE,"E8");var subQ2=makeQuery(id+"F0.imprint","INTERSECT",VERTEX,{"disambiguationData":[OD(0.0)],"derivedFrom":[subQ1,subQ0]});Q2=makeQuery(id+"F0.imprint","IMPRINT",FACE,{"disambiguationData":[TD([[makeQuery(id+"F0.imprint","IMPRINT",EDGE,{"disambiguationData":[TD([[subQ2,1.0]])],"derivedFrom":subQ1}),-1.0]])]});}
            var Q3;
            {var subQ0=sQuery(id+"F0.wireOp",EDGE,"E12");var subQ1=sQuery(id+"F0.wireOp",EDGE,"E8");var subQ2=makeQuery(id+"F0.imprint","INTERSECT",VERTEX,{"disambiguationData":[OD(0.0)],"derivedFrom":[subQ1,subQ0]});Q3=makeQuery(id+"F0.imprint","IMPRINT",FACE,{"disambiguationData":[TD([[makeQuery(id+"F0.imprint","IMPRINT",EDGE,{"disambiguationData":[TD([[subQ2,1.0]])],"derivedFrom":subQ1}),1.0]])]});}
            var Q4;
            Q4=makeQuery(id+"F0.imprint","IMPRINT",FACE,{"disambiguationData":[TD([[makeQuery(id+"F0.imprint","IMPRINT",EDGE,{"derivedFrom":sQuery(id+"F0.wireOp",EDGE,"E9")}),-1.0]])]});
            var Q5;
            Q5=sQuery(id+"F146yit5t1055Mi_29.wireOp",EDGE,"bMljMotk-M8YH-WNBY-laen-sy4S9EX9bsZt");
            var Q6;
            Q6=sQuery(id+"F146yit5t1055Mi_29.wireOp",EDGE,"93YKoeGf-wvDz-WYp3-dhvo-JkD2lF74KuC2");
            extrude(context, id + "F2", {"entities" : qUnion([Q0, Q1, Q2, Q3, Q4]), "surfaceEntities" : qUnion([Q5, Q6]), "oppositeDirection" : true, "depth" : 9 * mm, "offsetDistance" : 25 * mm});
        }
        {
            var Q0;
            Q0=qCreatedBy(makeId("Front.planeOp"),FACE);
            var sketch = newSketch(context, id + "F3", { "sketchPlane" : qUnion([Q0])});
            skLineSegment(sketch, "E18", {"start": v(0, 0) * mm, "end": v(0, 22.23) * mm});
            skSolve(sketch);
        }
        {
            var Q0;
            Q0=makeQuery(id+"F1.opExtrude","SWEPT_BODY",BODY,{"disambiguationData":[OSD([sQuery(id+"F0.wireOp",EDGE,"E0"),sQuery(id+"F0.wireOp",EDGE,"E2"),sQuery(id+"F0.wireOp",EDGE,"E3"),sQuery(id+"F0.wireOp",EDGE,"E6"),sQuery(id+"F0.wireOp",EDGE,"E7")])]});
            var Q1;
            Q1=sQuery(id+"F3.wireOp",EDGE,"E18");
            circularPattern(context, id + "F4", {"entities" : qUnion([Q0]), "axis" : qUnion([Q1]), "angle" : 360 * degree, "instanceCount" : 28, "equalSpace" : true});
        }
        {
            var Q0;
            Q0=makeQuery(id+"F0.imprint","IMPRINT",FACE,{"disambiguationData":[TD([[makeQuery(id+"F0.imprint","IMPRINT",EDGE,{"derivedFrom":sQuery(id+"F0.wireOp",EDGE,"E9")}),-1.0]])]});
            var Q1;
            {var subQ0=sQuery(id+"F0.wireOp",EDGE,"8zvVGQID-yt3e-UfqD-yb9D-NtDXdwGmcpxK");var subQ1=sQuery(id+"F0.wireOp",EDGE,"E8");var subQ2=makeQuery(id+"F0.imprint","INTERSECT",VERTEX,{"disambiguationData":[OD(0.0)],"derivedFrom":[subQ1,subQ0]});Q1=makeQuery(id+"F0.imprint","IMPRINT",FACE,{"disambiguationData":[TD([[makeQuery(id+"F0.imprint","IMPRINT",EDGE,{"disambiguationData":[TD([[subQ2,1.0]])],"derivedFrom":subQ1}),-1.0]])]});}
            var Q2;
            Q2=sQuery(id+"F0.wireOp",EDGE,"8zvVGQID-yt3e-UfqD-yb9D-NtDXdwGmcpxK");
            var Q3;
            Q3=sQuery(id+"F0.wireOp",EDGE,"E8");
            extrude(context, id + "F5", {"entities" : qUnion([Q0, Q1]), "operationType" : NewBodyOperationType.ADD, "surfaceEntities" : qUnion([Q2, Q3]), "oppositeDirection" : true, "depth" : 9 * mm, "offsetDistance" : 25 * mm});
        }
    });
